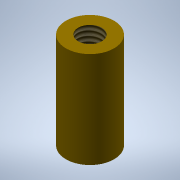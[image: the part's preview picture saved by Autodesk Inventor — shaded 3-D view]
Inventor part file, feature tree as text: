
AUTODESK INVENTOR PART (.ipt)
format: ipt  version: 2022.6 (Build 266554000, 554)  size: 115,712 bytes
history: native  units: mm
features: extrude x1, hole x1
ambient origin geometry x8: Origin, YZ Plane, XZ Plane, XY Plane, X Axis, Y Axis, Z Axis, Center Point
bodies: Solid1 (feature_tree)
feature tree (2):
  extrude  "Extrusion1"  Depth=5.0mm
  hole  "Hole1"  [1 undecoded]
note: 1 required parameter value undecoded (feature->parameter linkage not recoverable at this tier; creation-order binding heuristic only, values carry confidence <= 0.55)
